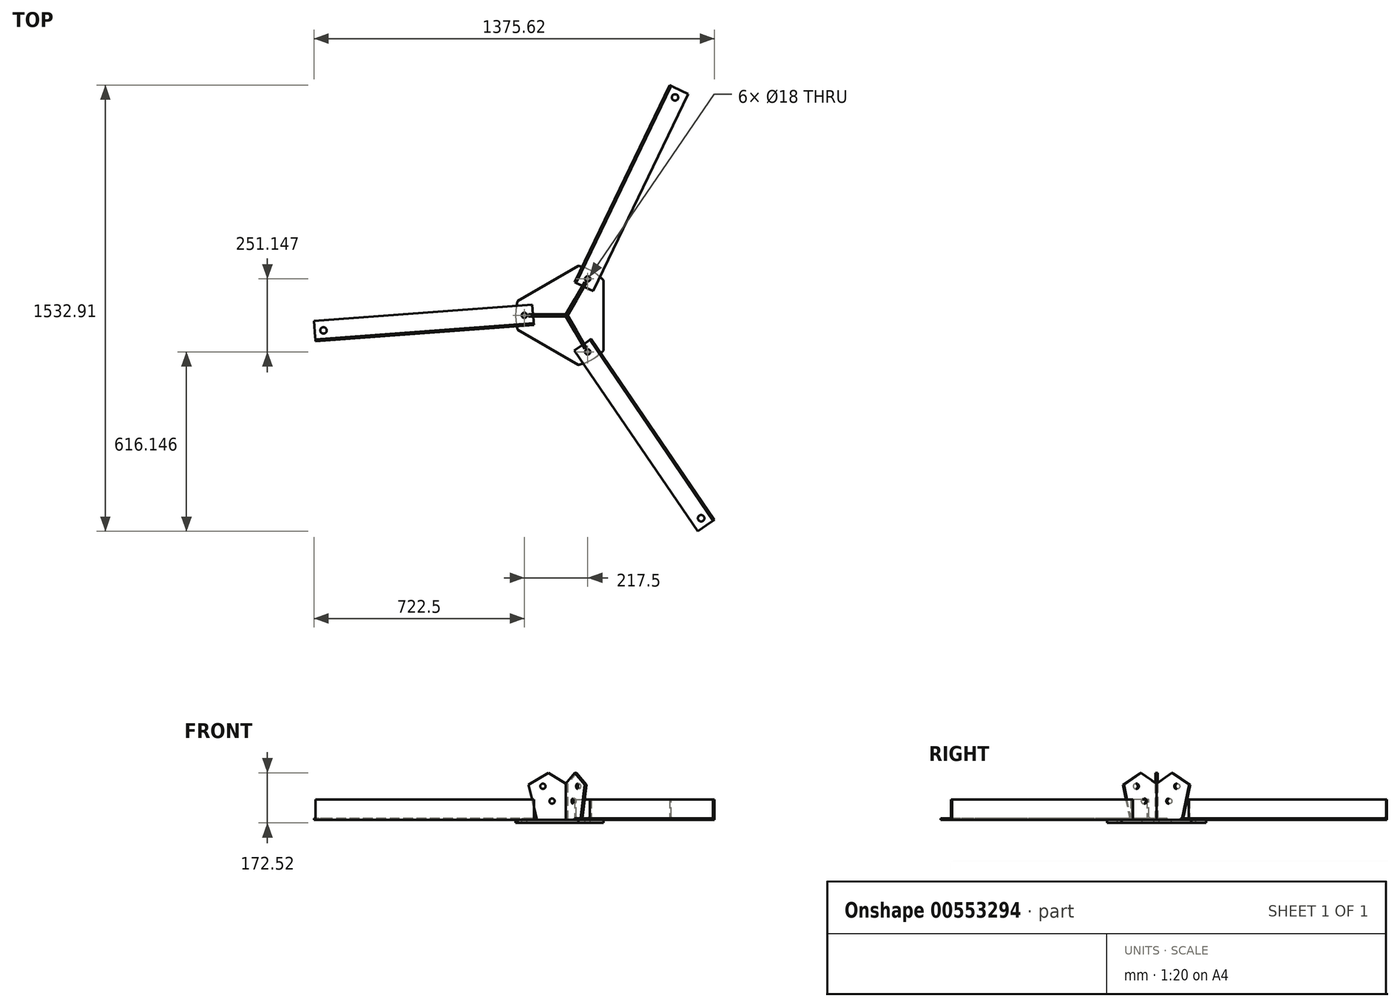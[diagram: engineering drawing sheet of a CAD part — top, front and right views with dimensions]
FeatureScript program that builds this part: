
annotation { "Feature Type Name" : "Feature", "Feature Type Description" : "" }
export const myFeature = defineFeature(function(context is Context, id is Id, definition is map)
    precondition{}
    {
        {
            var Q0;
            Q0=qCreatedBy(makeId("Top.planeOp"),FACE);
            var sketch = newSketch(context, id + "F0", { "sketchPlane" : qUnion([Q0])});
            skArc(sketch, "E0", {"start": v(40.55, -170.24) * mm, "mid": v(87.5, -151.55) * mm, "end": v(127.15, -120.24) * mm});
            skLineSegment(sketch, "E1", {"start": v(40.55, -170.24) * mm, "end": v(-167.7, -50) * mm});
            skLineSegment(sketch, "E2", {"start": v(0, 0) * mm, "end": v(-248.61, 0) * mm, "construction": true});
            skLineSegment(sketch, "E3.MirrorCS", {"start": v(40.55, 170.24) * mm, "end": v(-167.7, 50) * mm});
            skLineSegment(sketch, "E4", {"start": v(0, 0) * mm, "end": v(113.61, -196.78) * mm, "construction": true});
            skLineSegment(sketch, "E5.MirrorCS", {"start": v(127.15, -120.24) * mm, "end": v(127.15, 120.24) * mm});
            skArc(sketch, "E6.trimOffspring", {"start": v(-167.7, 50) * mm, "mid": v(-175, 0) * mm, "end": v(-167.7, -50) * mm});
            skArc(sketch, "E7.trimOffspring", {"start": v(127.15, 120.24) * mm, "mid": v(87.5, 151.55) * mm, "end": v(40.55, 170.24) * mm});
            skSolve(sketch);
        }
        {
            var Q0;
            Q0=makeQuery(id+"F0.imprint","IMPRINT",FACE,{"disambiguationData":[TD([[makeQuery(id+"F0.imprint","IMPRINT",EDGE,{"derivedFrom":sQuery(id+"F0.wireOp",EDGE,"E0")}),1.0]])]});
            extrude(context, id + "F1", {"entities" : qUnion([Q0]), "depth" : 10 * mm, "offsetDistance" : 25 * mm});
        }
        {
            var Q0;
            Q0=makeQuery(id+"F1.opExtrude","CAP_FACE",FACE,{"disambiguationData":[OSD([sQuery(id+"F0.wireOp",EDGE,"E0"),sQuery(id+"F0.wireOp",EDGE,"oJbW3ULZ-2pRP-CatU-Atqn-FDPEkCRfx0l3")])],"isStart":false});
            var sketch = newSketch(context, id + "F2", { "sketchPlane" : qUnion([Q0])});
            skCircle(sketch, "E8", {"center": v(-145, 0) * mm, "radius": 9 * mm});
            skCircle(sketch, "E9", {"center": v(72.5, -125.57) * mm, "radius": 9 * mm});
            skCircle(sketch, "E10", {"center": v(72.5, 125.57) * mm, "radius": 9 * mm});
            skCircle(sketch, "E11", {"center": v(0, 0) * mm, "radius": 145 * mm, "construction": true});
            skLineSegment(sketch, "E12", {"start": v(72.5, 125.57) * mm, "end": v(0, 0) * mm});
            skLineSegment(sketch, "E13", {"start": v(0, 0) * mm, "end": v(-145, 0) * mm});
            skLineSegment(sketch, "E14", {"start": v(0, 0) * mm, "end": v(72.5, -125.57) * mm});
            skSolve(sketch);
        }
        {
            var Q0;
            Q0=qSketchRegion(id+"F2",true);
            extrude(context, id + "F3", {"entities" : qUnion([Q0]), "operationType" : NewBodyOperationType.REMOVE, "oppositeDirection" : true, "depth" : 25 * mm, "offsetDistance" : 25 * mm});
        }
        {
            var Q0;
            Q0=makeQuery(id+"F1.opExtrude","CAP_FACE",FACE,{"disambiguationData":[OSD([sQuery(id+"F0.wireOp",EDGE,"E0")])],"isStart":false});
            var sketch = newSketch(context, id + "F4", { "sketchPlane" : qUnion([Q0])});
            skLineSegment(sketch, "E15", {"start": v(0, 0) * mm, "end": v(72.5, -125.57) * mm, "construction": true});
            skLineSegment(sketch, "E16", {"start": v(0, 0) * mm, "end": v(-145, 0) * mm, "construction": true});
            skLineSegment(sketch, "E17", {"start": v(0, 0) * mm, "end": v(72.5, 125.57) * mm, "construction": true});
            skLineSegment(sketch, "E18.0", {"start": v(-2.02, 3.5) * mm, "end": v(-74.92, 3.5) * mm});
            skLineSegment(sketch, "E18.1", {"start": v(-2.02, 3.5) * mm, "end": v(34.43, 66.63) * mm});
            skLineSegment(sketch, "E19.0", {"start": v(-2.02, -3.5) * mm, "end": v(-74.92, -3.5) * mm});
            skLineSegment(sketch, "E19.1", {"start": v(-2.02, -3.5) * mm, "end": v(34.47, -66.7) * mm});
            skLineSegment(sketch, "E20.0", {"start": v(4.04, 0) * mm, "end": v(40.53, -63.2) * mm});
            skLineSegment(sketch, "E20.1", {"start": v(4.04, 0) * mm, "end": v(40.5, 63.13) * mm});
            skLineSegment(sketch, "E21", {"start": v(40.53, -63.2) * mm, "end": v(34.47, -66.7) * mm});
            skLineSegment(sketch, "E22", {"start": v(40.5, 63.13) * mm, "end": v(34.43, 66.63) * mm});
            skCircle(sketch, "E23", {"center": v(0, 0) * mm, "radius": 75 * mm, "construction": true});
            skLineSegment(sketch, "E24", {"start": v(-74.92, -3.5) * mm, "end": v(-74.92, 3.5) * mm});
            skSolve(sketch);
        }
        {
            var Q0;
            Q0=qCreatedBy(makeId("Front.planeOp"),FACE);
            var sketch = newSketch(context, id + "F5", { "sketchPlane" : qUnion([Q0])});
            skLineSegment(sketch, "E25.trimOffspring", {"start": v(0, -16) * mm, "end": v(-925, -1374.5) * mm, "construction": true});
            skLineSegment(sketch, "E26", {"start": v(0, 0) * mm, "end": v(0, -32) * mm, "construction": true});
            skLineSegment(sketch, "E27", {"start": v(0, -16) * mm, "end": v(-196.24, -16) * mm, "construction": true});
            skLineSegment(sketch, "E28", {"start": v(-133.05, -149.22) * mm, "end": v(-65.51, -50.03) * mm, "construction": true});
            skLineSegment(sketch, "E29", {"start": v(-65.51, -50.03) * mm, "end": v(-7.65, -89.43) * mm, "construction": true});
            skLineSegment(sketch, "E30", {"start": v(-7.65, -89.43) * mm, "end": v(-75.2, -188.62) * mm, "construction": true});
            skCircle(sketch, "E31", {"center": v(-53.47, -94.53) * mm, "radius": 9 * mm});
            skCircle(sketch, "E32", {"center": v(-87.24, -144.12) * mm, "radius": 9 * mm});
            skLineSegment(sketch, "E33", {"start": v(-133.05, -149.22) * mm, "end": v(-75.2, -188.62) * mm, "construction": true});
            skLineSegment(sketch, "E34", {"start": v(-2.02, 0) * mm, "end": v(-102.02, 0) * mm});
            skLineSegment(sketch, "E35", {"start": v(-102.02, 0) * mm, "end": v(-137.18, -146.4) * mm});
            skLineSegment(sketch, "E36", {"start": v(-137.18, -146.4) * mm, "end": v(-71.06, -191.43) * mm});
            skLineSegment(sketch, "E37", {"start": v(-71.06, -191.43) * mm, "end": v(-2.02, -150) * mm});
            skLineSegment(sketch, "E38", {"start": v(-2.02, -150) * mm, "end": v(-2.02, 0) * mm});
            skSolve(sketch);
        }
        {
            var Q0;
            Q0=makeQuery(id+"F4.imprint","IMPRINT",FACE,{"disambiguationData":[TD([[makeQuery(id+"F4.imprint","IMPRINT",EDGE,{"derivedFrom":sQuery(id+"F4.wireOp",EDGE,"E18.0")}),1.0]])]});
            var sketch = newSketch(context, id + "F6", { "sketchPlane" : qUnion([Q0])});
            skLineSegment(sketch, "E39", {"start": v(-2.02, 3.5) * mm, "end": v(4.04, 0) * mm});
            skLineSegment(sketch, "E40", {"start": v(4.04, 0) * mm, "end": v(-2.02, -3.5) * mm});
            skLineSegment(sketch, "E41", {"start": v(-2.02, -3.5) * mm, "end": v(-2.02, 3.5) * mm});
            skSolve(sketch);
        }
        {
            var Q0;
            Q0=makeQuery(id+"F2.imprint","IMPRINT",FACE,{"disambiguationData":[TD([[makeQuery(id+"F2.imprint","IMPRINT",EDGE,{"derivedFrom":sQuery(id+"F2.wireOp",EDGE,"E8")}),-1.0]])]});
            var sketch = newSketch(context, id + "F7", { "sketchPlane" : qUnion([Q0])});
            skLineSegment(sketch, "E42", {"start": v(-115.08, 2.24) * mm, "end": v(-864.88, -54) * mm});
            skLineSegment(sketch, "E43", {"start": v(-145, 0) * mm, "end": v(-838.84, 0) * mm, "construction": true});
            skLineSegment(sketch, "E44", {"start": v(-838.84, 0) * mm, "end": v(-838.84, 0) * mm});
            skLineSegment(sketch, "E45", {"start": v(-838.84, 0) * mm, "end": v(-834.96, -51.75) * mm, "construction": true});
            skSolve(sketch);
        }
        {
            var Q0;
            Q0=sQuery(id+"F7.wireOp",VERTEX,"E42.start");
            var Q1;
            Q1=sQuery(id+"F7.wireOp",EDGE,"E42");
            cPlane(context, id + "F8", {"entities" : qUnion([Q0, Q1]), "cplaneType" : CPlaneType.LINE_POINT, "offset" : 25 * mm, "width" : 150 * mm, "height" : 150 * mm});
        }
        {
            var Q0;
            Q0=qCreatedBy(id+"F8.planeOp",FACE);
            var sketch = newSketch(context, id + "F9", { "sketchPlane" : qUnion([Q0])});
            skLineSegment(sketch, "E46", {"start": v(24.15, 10) * mm, "end": v(-45.85, 10) * mm});
            skLineSegment(sketch, "E47", {"start": v(-45.85, 10) * mm, "end": v(-45.85, 16) * mm});
            skLineSegment(sketch, "E48", {"start": v(-45.85, 16) * mm, "end": v(10.15, 16) * mm});
            skLineSegment(sketch, "E49", {"start": v(18.15, 24) * mm, "end": v(18.15, 80) * mm});
            skLineSegment(sketch, "E50", {"start": v(18.15, 80) * mm, "end": v(24.15, 80) * mm});
            skLineSegment(sketch, "E51", {"start": v(24.15, 80) * mm, "end": v(24.15, 10) * mm});
            skPoint(sketch, "E52.visualSharp", {"position": v(18.15, 16) * mm});
            skArc(sketch, "E52.filletArc", {"start": v(10.15, 16) * mm, "mid": v(15.81, 18.34) * mm, "end": v(18.15, 24) * mm});
            skSolve(sketch);
        }
        {
            var Q0;
            Q0=qSketchRegion(id+"F9",true);
            var Q1;
            Q1=sQuery(id+"F7.wireOp",EDGE,"E42");
            sweep(context, id + "F10", {"profiles" : qUnion([Q0]), "path" : qUnion([Q1])});
        }
        {
            var Q0;
            Q0=makeQuery(id+"F10.opSweep","SWEPT_FACE",FACE,{"disambiguationData":[OSD([sQuery(id+"F7.wireOp",EDGE,"E42"),sQuery(id+"F9.wireOp",EDGE,"E48")])]});
            var sketch = newSketch(context, id + "F11", { "sketchPlane" : qUnion([Q0])});
            skCircle(sketch, "E53.0", {"center": v(-145, 0) * mm, "radius": 9 * mm});
            skLineSegment(sketch, "E54", {"start": v(-492.6, 9.02) * mm, "end": v(-492.64, 9.59) * mm, "construction": true});
            skCircle(sketch, "E55.MirrorC", {"center": v(-834.96, -51.75) * mm, "radius": 9 * mm, "construction": true});
            skCircle(sketch, "E56", {"center": v(-834.96, -51.75) * mm, "radius": 11 * mm});
            skSolve(sketch);
        }
        {
            var Q0;
            Q0=sQuery(id+"F11.wireOp",VERTEX,"E53.0.center");
            var Q1;
            Q1=makeQuery(id+"F10.opSweep","SWEPT_BODY",BODY,{"disambiguationData":[OSD([sQuery(id+"F7.wireOp",EDGE,"E42"),sQuery(id+"F9.wireOp",EDGE,"E46"),sQuery(id+"F9.wireOp",EDGE,"E47"),sQuery(id+"F9.wireOp",EDGE,"E48"),sQuery(id+"F9.wireOp",EDGE,"E49"),sQuery(id+"F9.wireOp",EDGE,"E50"),sQuery(id+"F9.wireOp",EDGE,"E51"),sQuery(id+"F9.wireOp",EDGE,"E52.filletArc")])]});
            hole(context, id + "F12", {"style" : HoleStyle.SIMPLE, "endStyle" : HoleEndStyle.BLIND, "holeDiameter" : 18 * mm, "majorDiameter" : 5 * mm, "holeDepth" : 22 * mm, "isTappedThrough" : true, "tappedDepth" : 12 * mm, "tapClearance" : 3, "locations" : qUnion([Q0]), "scope" : qUnion([Q1]), "startStyle" : HoleStartStyle.PART});
        }
        {
            var Q0;
            Q0=sQuery(id+"F7.wireOp",VERTEX,"E45.end");
            var Q1;
            Q1=makeQuery(id+"F10.opSweep","SWEPT_BODY",BODY,{"disambiguationData":[OSD([sQuery(id+"F7.wireOp",EDGE,"E42"),sQuery(id+"F9.wireOp",EDGE,"E46"),sQuery(id+"F9.wireOp",EDGE,"E47"),sQuery(id+"F9.wireOp",EDGE,"E48"),sQuery(id+"F9.wireOp",EDGE,"E49"),sQuery(id+"F9.wireOp",EDGE,"E50"),sQuery(id+"F9.wireOp",EDGE,"E51"),sQuery(id+"F9.wireOp",EDGE,"E52.filletArc")])]});
            hole(context, id + "F13", {"style" : HoleStyle.SIMPLE, "endStyle" : HoleEndStyle.BLIND, "oppositeDirection" : true, "holeDiameter" : 22 * mm, "majorDiameter" : 5 * mm, "holeDepth" : 22 * mm, "isTappedThrough" : true, "tappedDepth" : 12 * mm, "tapClearance" : 3, "locations" : qUnion([Q0]), "scope" : qUnion([Q1]), "startStyle" : HoleStartStyle.PART});
        }
        {
            var Q0;
            Q0=makeQuery(id+"F10.opSweep","SWEPT_BODY",BODY,{"disambiguationData":[OSD([sQuery(id+"F7.wireOp",EDGE,"E42"),sQuery(id+"F9.wireOp",EDGE,"E46"),sQuery(id+"F9.wireOp",EDGE,"E47"),sQuery(id+"F9.wireOp",EDGE,"E48"),sQuery(id+"F9.wireOp",EDGE,"E49"),sQuery(id+"F9.wireOp",EDGE,"E50"),sQuery(id+"F9.wireOp",EDGE,"E51"),sQuery(id+"F9.wireOp",EDGE,"E52.filletArc")])]});
            var Q1;
            Q1=sQuery(id+"F4.wireOp",EDGE,"E23");
            circularPattern(context, id + "F14", {"entities" : qUnion([Q0]), "axis" : qUnion([Q1]), "angle" : 360 * degree, "instanceCount" : 3, "equalSpace" : true, "computeTransformsWithoutBuiltin" : true});
        }
        {
            var Q0;
            Q0=qCreatedBy(makeId("Front.planeOp"),FACE);
            var sketch = newSketch(context, id + "F15", { "sketchPlane" : qUnion([Q0])});
            skLineSegment(sketch, "E57", {"start": v(-2.02, 10) * mm, "end": v(-102.02, 10) * mm});
            skLineSegment(sketch, "E58", {"start": v(-102.02, 10) * mm, "end": v(-130.9, 130.66) * mm});
            skLineSegment(sketch, "E59", {"start": v(-130.9, 130.66) * mm, "end": v(-62.74, 172.52) * mm});
            skLineSegment(sketch, "E60", {"start": v(-62.74, 172.52) * mm, "end": v(-2.02, 135) * mm});
            skLineSegment(sketch, "E61", {"start": v(-2.02, 135) * mm, "end": v(-2.02, 10) * mm});
            skLineSegment(sketch, "E62", {"start": v(-3.72, 0) * mm, "end": v(-925, 1500) * mm, "construction": true});
            skLineSegment(sketch, "E63", {"start": v(-126.65, 133.27) * mm, "end": v(-63.85, 31.02) * mm, "construction": true});
            skLineSegment(sketch, "E64", {"start": v(-63.85, 31.02) * mm, "end": v(-4.2, 67.65) * mm, "construction": true});
            skLineSegment(sketch, "E65", {"start": v(-4.2, 67.65) * mm, "end": v(-67, 169.9) * mm, "construction": true});
            skLineSegment(sketch, "E66", {"start": v(-67, 169.9) * mm, "end": v(-126.65, 133.27) * mm, "construction": true});
            skCircle(sketch, "E67", {"center": v(-49.72, 74.9) * mm, "radius": 9 * mm});
            skCircle(sketch, "E68", {"center": v(-81.12, 126.03) * mm, "radius": 9 * mm});
            skSolve(sketch);
        }
        {
            var Q0;
            Q0=qSketchRegion(id+"F15",true);
            extrude(context, id + "F16", {"entities" : qUnion([Q0]), "depth" : 7 * mm, "offsetDistance" : 25 * mm, "symmetric" : true});
        }
        {
            var Q0;
            Q0=makeQuery(id+"F16.opExtrude","SWEPT_BODY",BODY,{"disambiguationData":[OSD([sQuery(id+"F15.wireOp",EDGE,"E57"),sQuery(id+"F15.wireOp",EDGE,"E58"),sQuery(id+"F15.wireOp",EDGE,"E59"),sQuery(id+"F15.wireOp",EDGE,"E60"),sQuery(id+"F15.wireOp",EDGE,"E61"),sQuery(id+"F15.wireOp",EDGE,"E67"),sQuery(id+"F15.wireOp",EDGE,"E68")])]});
            var Q1;
            Q1=sQuery(id+"F4.wireOp",EDGE,"E23");
            circularPattern(context, id + "F17", {"entities" : qUnion([Q0]), "axis" : qUnion([Q1]), "angle" : 360 * degree, "instanceCount" : 3, "equalSpace" : true, "computeTransformsWithoutBuiltin" : true});
        }
        {
            var Q0;
            Q0=makeQuery(id+"F7.imprint","IMPRINT",FACE,{"disambiguationData":[TD([[makeQuery(id+"F7.imprint","IMPRINT",EDGE,{"derivedFrom":makeQuery(id+"F2.imprint","IMPRINT",EDGE,{"derivedFrom":sQuery(id+"F2.wireOp",EDGE,"E9")})}),-1.0]])]});
            var sketch = newSketch(context, id + "F18", { "sketchPlane" : qUnion([Q0])});
            skLineSegment(sketch, "E69.0", {"start": v(4.04, 0) * mm, "end": v(-2.02, -3.5) * mm});
            skLineSegment(sketch, "E69.1", {"start": v(-2.02, -3.5) * mm, "end": v(-2.02, 3.5) * mm});
            skLineSegment(sketch, "E69.2", {"start": v(-2.02, 3.5) * mm, "end": v(4.04, 0) * mm});
            skSolve(sketch);
        }
        {
            var Q0;
            Q0=qSketchRegion(id+"F18",true);
            var Q1;
            Q1=makeQuery(id+"F17.opPattern","COPY",VERTEX,{"derivedFrom":makeQuery(id+"F16.opExtrude","CAP_VERTEX",VERTEX,{"disambiguationData":[OSD([sQuery(id+"F15.wireOp",EDGE,"E60"),sQuery(id+"F15.wireOp",EDGE,"E61")])],"isStart":true}),"instanceName":"2"});
            extrude(context, id + "F19", {"entities" : qUnion([Q0]), "operationType" : NewBodyOperationType.ADD, "endBound" : BoundingType.UP_TO_VERTEX, "depth" : 25 * mm, "endBoundEntityVertex" : qUnion([Q1]), "offsetDistance" : 25 * mm});
        }
        {
            var Q0;
            Q0=makeQuery(id+"F0.imprint","IMPRINT",FACE,{"disambiguationData":[TD([[makeQuery(id+"F0.imprint","IMPRINT",EDGE,{"derivedFrom":sQuery(id+"F0.wireOp",EDGE,"E0")}),1.0]])]});
            cPlane(context, id + "F20", {"entities" : qUnion([Q0]), "cplaneType" : CPlaneType.OFFSET, "offset" : 8 * mm, "oppositeDirection" : true, "width" : 150 * mm, "height" : 150 * mm});
        }
    });
